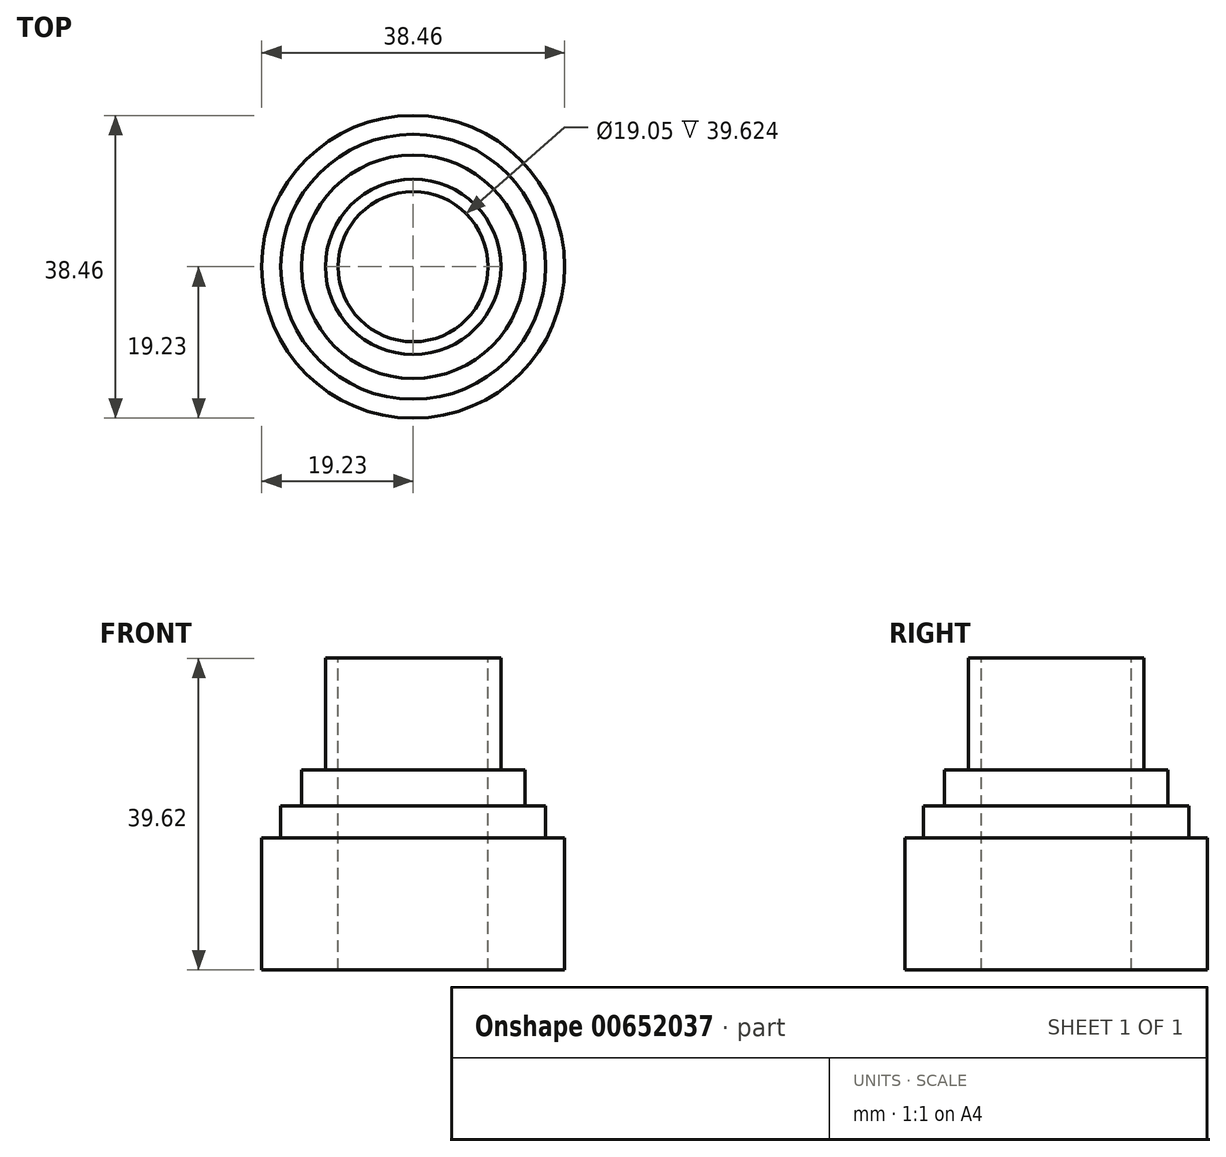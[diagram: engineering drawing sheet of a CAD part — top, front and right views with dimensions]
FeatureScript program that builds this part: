
annotation { "Feature Type Name" : "Feature", "Feature Type Description" : "" }
export const myFeature = defineFeature(function(context is Context, id is Id, definition is map)
    precondition{}
    {
        {
            var Q0;
            Q0=qCreatedBy(makeId("Top.planeOp"),FACE);
            var sketch = newSketch(context, id + "F0", { "sketchPlane" : qUnion([Q0])});
            skCircle(sketch, "E0", {"center": v(0, 0) * mm, "radius": 19.23 * mm});
            skSolve(sketch);
        }
        {
            var Q0;
            Q0 = qSketchRegion(id + "F0", true);
            extrude(context, id + "F1", {"entities" : qUnion([Q0]), "depth" : 16.76 * mm, "offsetDistance" : 25.4 * mm});
        }
        {
            var Q0;
            Q0=qCreatedBy(makeId("Top.planeOp"),FACE);
            var sketch = newSketch(context, id + "F2", { "sketchPlane" : qUnion([Q0])});
            skCircle(sketch, "E1", {"center": v(0, 0) * mm, "radius": 16.83 * mm});
            skSolve(sketch);
        }
        {
            var Q0;
            Q0 = qSketchRegion(id + "F2", true);
            extrude(context, id + "F3", {"entities" : qUnion([Q0]), "operationType" : NewBodyOperationType.ADD, "depth" : 20.83 * mm, "offsetDistance" : 25.4 * mm});
        }
        {
            var Q0;
            Q0=qCreatedBy(makeId("Top.planeOp"),FACE);
            var sketch = newSketch(context, id + "F4", { "sketchPlane" : qUnion([Q0])});
            skCircle(sketch, "E2", {"center": v(0, 0) * mm, "radius": 14.2 * mm});
            skSolve(sketch);
        }
        {
            var Q0;
            Q0 = qSketchRegion(id + "F4", true);
            extrude(context, id + "F5", {"entities" : qUnion([Q0]), "operationType" : NewBodyOperationType.ADD, "depth" : 25.4 * mm, "offsetDistance" : 25.4 * mm});
        }
        {
            var Q0;
            Q0=qCreatedBy(makeId("Top.planeOp"),FACE);
            var sketch = newSketch(context, id + "F6", { "sketchPlane" : qUnion([Q0])});
            skCircle(sketch, "E3", {"center": v(0, 0) * mm, "radius": 11.14 * mm});
            skSolve(sketch);
        }
        {
            var Q0;
            Q0 = qSketchRegion(id + "F6", true);
            extrude(context, id + "F7", {"entities" : qUnion([Q0]), "operationType" : NewBodyOperationType.ADD, "depth" : 39.62 * mm, "offsetDistance" : 25.4 * mm});
        }
        {
            var Q0;
            Q0=makeQuery(id+"F7.opExtrude","CAP_FACE",FACE,{"disambiguationData":[OSD([sQuery(id+"F6.wireOp",EDGE,"E3")])],"isStart":false});
            var sketch = newSketch(context, id + "F8", { "sketchPlane" : qUnion([Q0])});
            skCircle(sketch, "E4", {"center": v(0, 0) * mm, "radius": 9.34 * mm});
            skSolve(sketch);
        }
        {
            var Q0;
            Q0=sQuery(id+"F8.wireOp",VERTEX,"E4.center");
            var Q1;
            Q1=makeQuery(id+"F1.opExtrude","SWEPT_BODY",BODY,{"disambiguationData":[OSD([sQuery(id+"F0.wireOp",EDGE,"E0")])]});
            hole(context, id + "F9", {"style" : HoleStyle.SIMPLE, "endStyle" : HoleEndStyle.THROUGH, "holeDiameter" : 19.05 * mm, "majorDiameter" : 6.35 * mm, "isTappedThrough" : true, "tappedDepth" : 12.7 * mm, "tapClearance" : 3, "locations" : qUnion([Q0]), "scope" : qUnion([Q1])});
        }
    });
